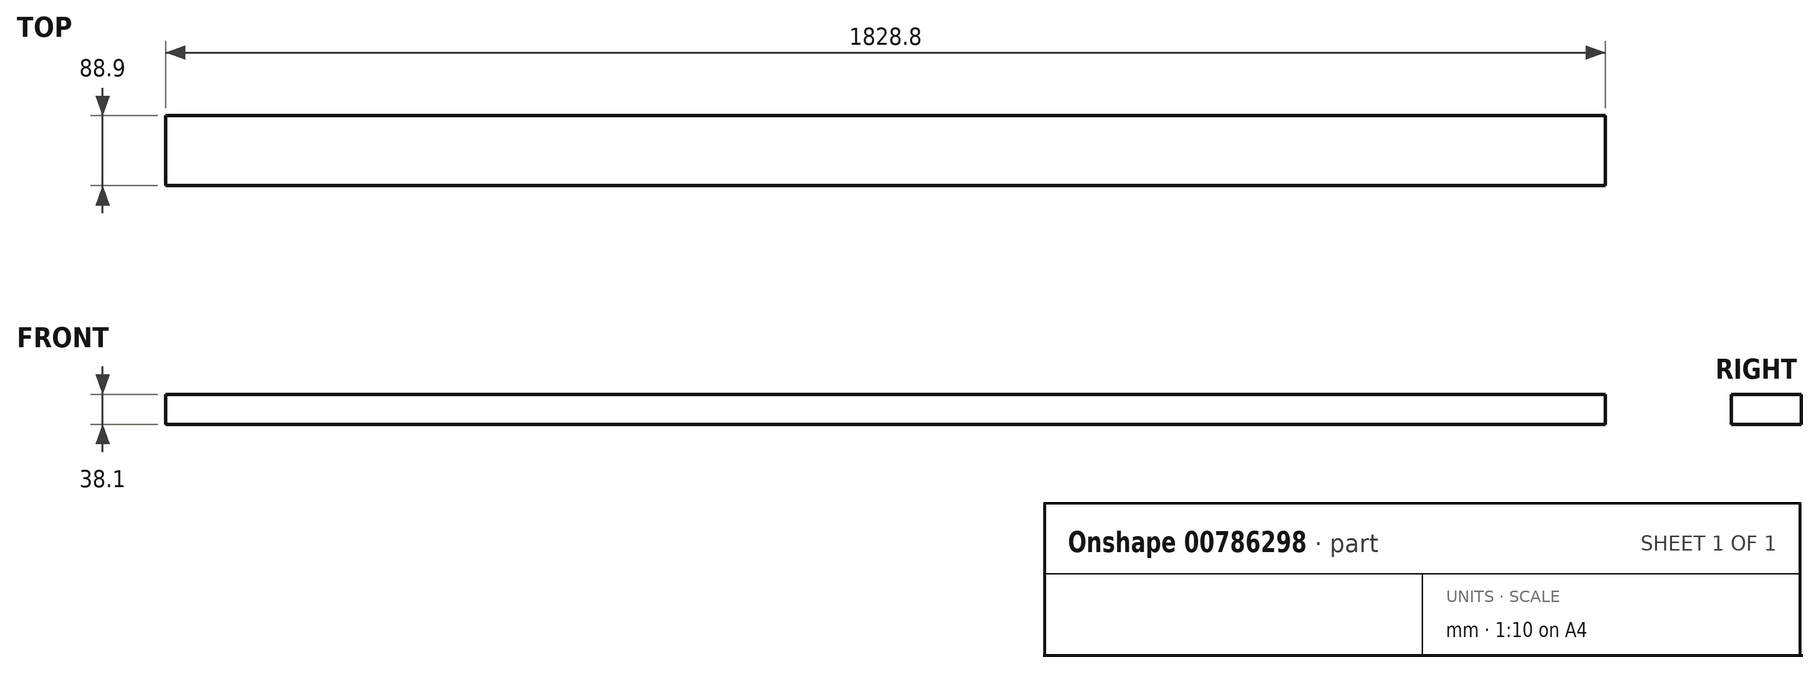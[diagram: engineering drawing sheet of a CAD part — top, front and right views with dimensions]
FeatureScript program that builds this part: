
annotation { "Feature Type Name" : "Feature", "Feature Type Description" : "" }
export const myFeature = defineFeature(function(context is Context, id is Id, definition is map)
    precondition{}
    {
        {
            var Q0;
            Q0=qCreatedBy(makeId("Front.planeOp"),FACE);
            var sketch = newSketch(context, id + "F0", { "sketchPlane" : qUnion([Q0])});
            skLineSegment(sketch, "E0.bottom", {"start": v(-914.4, 19.05) * mm, "end": v(914.4, 19.05) * mm});
            skLineSegment(sketch, "E0.top", {"start": v(-914.4, -19.05) * mm, "end": v(914.4, -19.05) * mm});
            skLineSegment(sketch, "E0.left", {"start": v(-914.4, 19.05) * mm, "end": v(-914.4, -19.05) * mm});
            skLineSegment(sketch, "E0.right", {"start": v(914.4, 19.05) * mm, "end": v(914.4, -19.05) * mm});
            skPoint(sketch, "E0.middle", {"position": v(0, 0) * mm});
            skSolve(sketch);
        }
        {
            var Q0;
            Q0=makeQuery(id+"F0.imprint","IMPRINT",FACE,{"disambiguationData":[TD([[makeQuery(id+"F0.imprint","IMPRINT",EDGE,{"derivedFrom":sQuery(id+"F0.wireOp",EDGE,"E0.bottom")}),-1.0]])]});
            extrude(context, id + "F1", {"entities" : qUnion([Q0]), "endBound" : BoundingType.SYMMETRIC, "depth" : 88.9 * mm, "offsetDistance" : 25.4 * mm});
        }
    });
